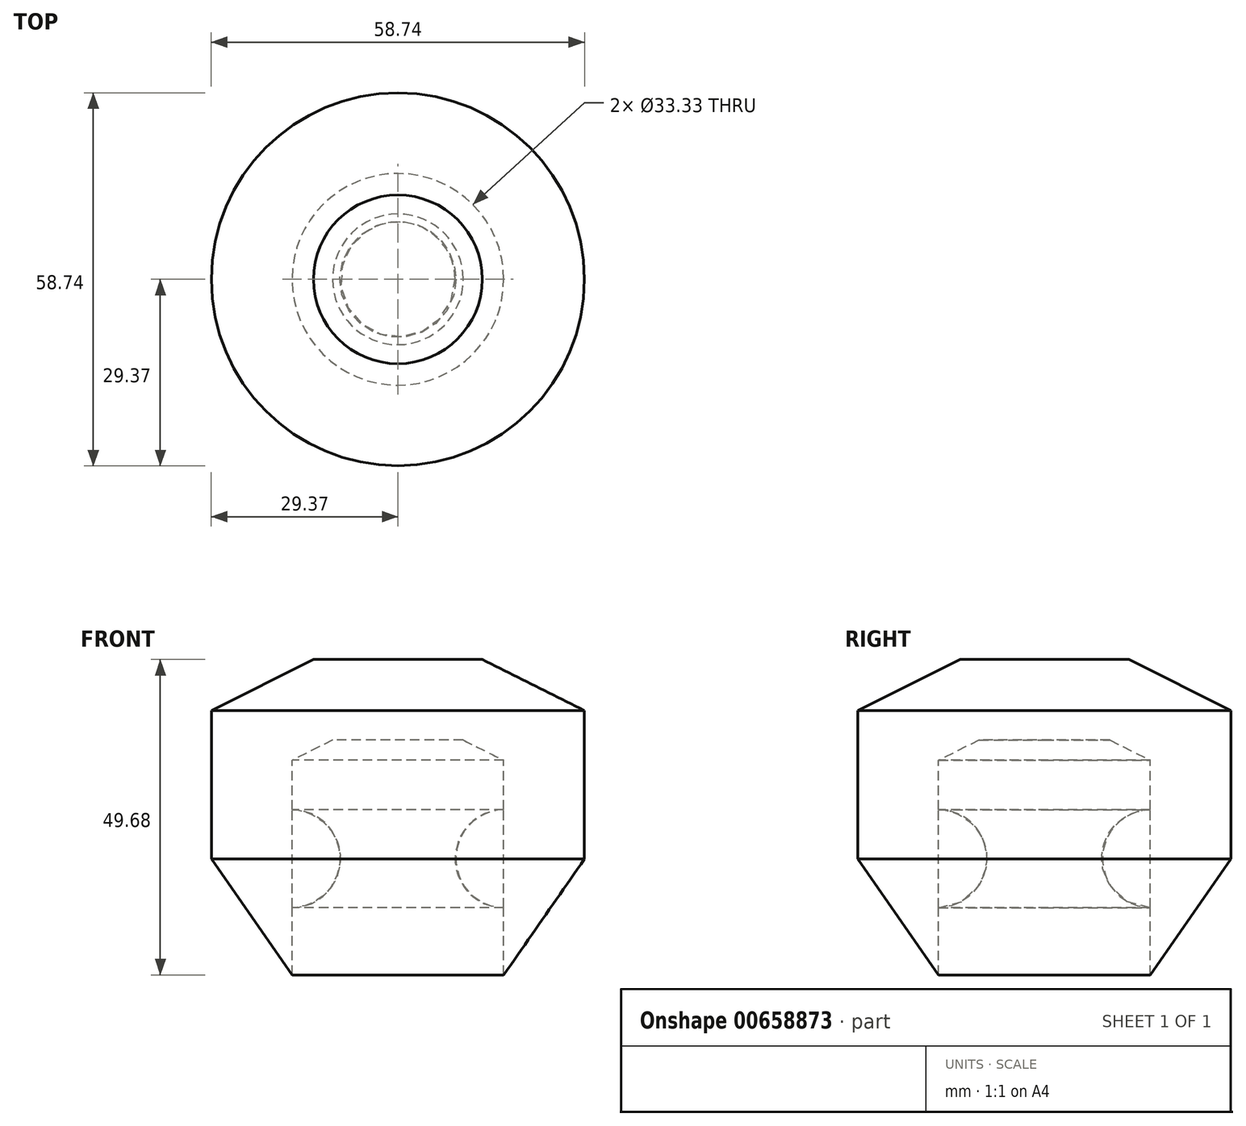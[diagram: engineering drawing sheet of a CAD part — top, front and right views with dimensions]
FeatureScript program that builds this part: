
annotation { "Feature Type Name" : "Feature", "Feature Type Description" : "" }
export const myFeature = defineFeature(function(context is Context, id is Id, definition is map)
    precondition{}
    {
        {
            var Q0;
            Q0=qCreatedBy(makeId("Front.planeOp"),FACE);
            var sketch = newSketch(context, id + "F0", { "sketchPlane" : qUnion([Q0])});
            skLineSegment(sketch, "E0", {"start": v(-29.37, 0) * mm, "end": v(-29.37, 23.4) * mm});
            skLineSegment(sketch, "E1", {"start": v(-29.37, 23.4) * mm, "end": v(-13.29, 31.44) * mm});
            skLineSegment(sketch, "E2", {"start": v(-13.29, 31.44) * mm, "end": v(0, 31.44) * mm});
            skLineSegment(sketch, "E3.MirrorCS", {"start": v(13.29, 31.44) * mm, "end": v(0, 31.44) * mm});
            skLineSegment(sketch, "E4.MirrorCS", {"start": v(29.37, 23.4) * mm, "end": v(13.29, 31.44) * mm});
            skLineSegment(sketch, "E5.MirrorCS", {"start": v(29.37, 0) * mm, "end": v(29.37, 23.4) * mm});
            skLineSegment(sketch, "E6.0", {"start": v(16.67, 0) * mm, "end": v(16.67, 15.55) * mm});
            skLineSegment(sketch, "E6.1", {"start": v(16.67, 15.55) * mm, "end": v(10.29, 18.74) * mm});
            skLineSegment(sketch, "E6.2", {"start": v(-16.67, 0) * mm, "end": v(-16.67, 15.55) * mm});
            skLineSegment(sketch, "E6.3", {"start": v(-16.67, 15.55) * mm, "end": v(-10.29, 18.74) * mm});
            skLineSegment(sketch, "E6.4", {"start": v(-10.29, 18.74) * mm, "end": v(0, 18.74) * mm});
            skLineSegment(sketch, "E6.5", {"start": v(10.29, 18.74) * mm, "end": v(0, 18.74) * mm});
            skLineSegment(sketch, "E7", {"start": v(-16.67, 0) * mm, "end": v(-16.67, -18.24) * mm});
            skLineSegment(sketch, "E8", {"start": v(-29.37, 0) * mm, "end": v(-16.67, -18.24) * mm});
            skLineSegment(sketch, "E9", {"start": v(16.67, 0) * mm, "end": v(16.67, -18.24) * mm});
            skLineSegment(sketch, "E10", {"start": v(29.37, 0) * mm, "end": v(16.67, -18.24) * mm});
            skArc(sketch, "E11", {"start": v(16.67, 7.78) * mm, "mid": v(9.02, 0.06) * mm, "end": v(16.67, -7.67) * mm});
            skArc(sketch, "E12", {"start": v(-16.67, -7.67) * mm, "mid": v(-9.14, 0.06) * mm, "end": v(-16.67, 7.78) * mm});
            skLineSegment(sketch, "E13", {"start": v(0, 37.34) * mm, "end": v(0, -26.08) * mm});
            skSolve(sketch);
        }
        {
            var Q0;
            Q0=makeQuery(id+"F0.imprint","IMPRINT",FACE,{"disambiguationData":[TD([[makeQuery(id+"F0.imprint","IMPRINT",EDGE,{"derivedFrom":sQuery(id+"F0.wireOp",EDGE,"E0")}),-1.0]])]});
            var Q1;
            {var subQ3=sQuery(id+"F0.wireOp",EDGE,"E12");Q1=makeQuery(id+"F0.imprint","IMPRINT",FACE,{"disambiguationData":[TD([[makeQuery(id+"F0.imprint","IMPRINT",EDGE,{"derivedFrom":subQ3}),1.0]])]});}
            var Q2;
            {var subQ3=sQuery(id+"F0.wireOp",EDGE,"E11");Q2=makeQuery(id+"F0.imprint","IMPRINT",FACE,{"disambiguationData":[TD([[makeQuery(id+"F0.imprint","IMPRINT",EDGE,{"derivedFrom":subQ3}),1.0]])]});}
            var Q3;
            Q3=sQuery(id+"F0.wireOp",EDGE,"E13");
            revolve(context, id + "F1", {"entities" : qUnion([Q0, Q1, Q2]), "axis" : qUnion([Q3]), "revolveType" : RevolveType.FULL});
        }
    });
